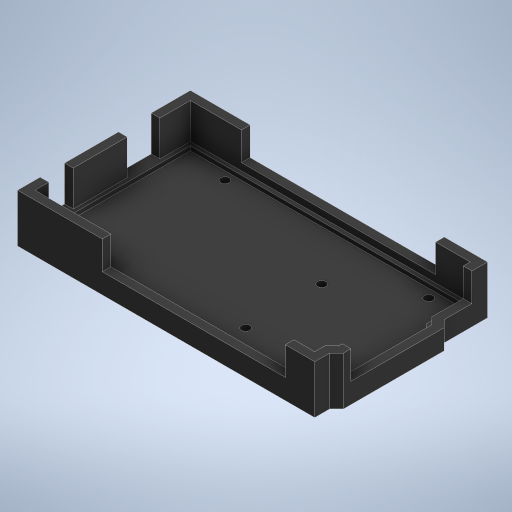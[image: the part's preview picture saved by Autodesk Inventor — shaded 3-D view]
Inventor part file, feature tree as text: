
AUTODESK INVENTOR PART (.ipt)
format: ipt  version: 2024 (Build 280153000, 153)  size: 564,736 bytes
history: native  units: in
note: dims shown in document units (in); Inventor stores cm internally (conversion verified against a paired STEP export)
features: sketch x7, extrude x5, mirror x1
ambient origin geometry x8: Origin, YZ Plane, XZ Plane, XY Plane, X Axis, Y Axis, Z Axis, Center Point
bodies: Solid1 (feature_tree)
feature tree (13):
  sketch  "Sketch1"  dims[d0=2.1in d1=0.125in]
  extrude  "Extrusion1"  Depth=0.125in
  extrude  "Extrusion2"  Depth=0.3543in
  extrude  "Extrusion3"  Depth=0.25in
  extrude  "Extrusion4"  Depth=0.474in
  mirror  "Mirror1"
  extrude  "Extrusion5"  Depth=0.5382in
  sketch  "Sketch6"  dims[d10=0.1in]
  sketch  "Sketch7"  dims[d11=0.6in d12=0.1in d13=0.35in d14=0.1in d15=0.1in d16=0.1in d17=0.7in d18=1.3in d19=1.3in d20=0.3in d21=0.51in d22=0.1in d23=0.1in d24=0.1in d25=0.1in d26=0.1in d27=0.125in d28=0.125in d29=0.125in d30=0.125in d31=0.125in d32=0.125in d33=0.2in d34=0.125in d35=0.2in d36=0.125in d37=2.1in d38=0.125in d39=0.075in d40=0.3543in d41=0.3661in d42=0.25in d43=0.474in d44=3.9in d45=3.9in d46=0.5382in d47=0.1in d48=0.6in d49=0.1in d50=0.35in d51=0.1in d52=0.1in d53=0.1in d54=0.7in d55=1.3in d56=1.3in d57=0.3in d58=0.51in d59=0.1in d60=0.1in d61=0.1in d62=0.1in d63=0.1in d64=0.125in d65=0.125in d66=0.125in d67=0.125in d68=0.125in d69=0.125in d70=0.2in d71=0.125in d72=0.2in d73=0.125in d74=2.1in d75=0.125in d76=0.075in d77=0.3543in d78=0.3661in d79=0.25in d80=0.474in d81=3.9in d82=3.9in d83=0.5382in d84=0.1in d85=0.6in d86=0.1in d87=0.35in d88=0.1in d89=0.1in d90=0.1in d91=0.7in d92=1.3in d93=1.3in d94=0.3in d95=0.51in d96=0.1in d97=0.1in d98=0.1in d99=0.1in d100=0.1in d101=0.125in d102=0.125in d103=0.125in d104=0.125in d105=0.125in d106=0.125in d107=0.2in d108=0.125in d109=0.2in d110=0.125in d111=2.1in d112=0.125in d113=0.075in d114=0.3543in d115=0.3661in d116=0.25in d117=0.474in d118=3.9in d119=3.9in d120=0.5382in d121=0.1in d122=0.6in d123=0.1in d124=0.35in d125=0.1in d126=0.1in d127=0.1in d128=0.7in d129=1.3in d130=1.3in d131=0.3in d132=0.51in d133=0.1in d134=0.1in d135=0.1in d136=0.1in d137=0.1in d138=0.125in d139=0.125in d140=0.125in d141=0.125in d142=0.125in d143=0.125in d144=0.2in d145=0.125in d146=0.2in d147=0.125in d148=2.1in d149=0.125in d150=0.075in d151=0.3543in d152=0.3661in d153=0.25in d154=0.474in d155=3.9in d156=3.9in d157=0.5382in d158=0.1in d159=0.6in d160=0.1in d161=0.35in d162=0.1in d163=0.1in d164=0.1in d165=0.7in d166=1.3in d167=1.3in d168=0.3in d169=0.51in d170=0.1in d171=0.1in d172=0.1in d173=0.1in d174=0.1in d175=0.125in d176=0.125in d177=0.125in d178=0.125in d179=0.125in d180=0.125in d181=0.2in d182=0.125in d183=0.2in d184=0.125in d185=0.125in d186=0.0in d187=0.0625in d188=0.0in d189=0.5756in d190=0.0in d191=0.75in d192=0.0in d193=1.225in d194=2.65in d195=0.865in d196=2.81in d197=0.225in d198=1.85in d199=0.41in d200=0.0in]
  sketch  "Sketch2"  dims[d2=0.075in d3=0.3543in]
  sketch  "Sketch3"  dims[d4=0.3661in d5=0.25in]
  sketch  "Sketch4"  dims[d6=0.474in d7=3.9in]
  sketch  "Sketch5"  dims[d8=3.9in d9=0.5382in]
